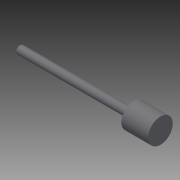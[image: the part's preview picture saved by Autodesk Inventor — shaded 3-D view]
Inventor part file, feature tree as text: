
AUTODESK INVENTOR PART (.ipt)
format: ipt  version: 2014 (Build 180170000, 170)  size: 115,712 bytes
history: native  units: in
note: dims shown in document units (in); Inventor stores cm internally (conversion verified against a paired STEP export)
features: other x49, revolve x2, sketch x2
ambient origin geometry x8: Origin, YZ Plane, XZ Plane, XY Plane, X Axis, Y Axis, Z Axis, Center Point
bodies: Solid1 (feature_tree)
feature tree (53):
  revolve  "Revolution1"  Angle=360.0deg
  revolve  "Revolution2"  [1 undecoded]
  other  "h1_XY"
  other  "h1_YZ"
  other  "h1_ZX"
  other  "h1_X"
  other  "h1_Y"
  other  "h1_Z"
  other  "h1_Center"
  other  "h2_XY"
  other  "h2_YZ"
  other  "h2_ZX"
  other  "h2_X"
  other  "h2_Y"
  other  "h2_Z"
  other  "h2_Center"
  other  "k1_XY"
  other  "k1_YZ"
  other  "k1_ZX"
  other  "k1_X"
  other  "k1_Y"
  other  "k1_Z"
  other  "k1_Center"
  other  "k2_XY"
  other  "k2_YZ"
  other  "k2_ZX"
  other  "k2_X"
  other  "k2_Y"
  other  "k2_Z"
  other  "k2_Center"
  other  "start_XY"
  other  "start_YZ"
  other  "start_ZX"
  other  "start_X"
  other  "start_Y"
  other  "start_Z"
  other  "start_Center"
  other  "to_prc_XY"
  other  "to_prc_YZ"
  other  "to_prc_ZX"
  other  "to_prc_X"
  other  "to_prc_Y"
  other  "to_prc_Z"
  other  "to_prc_Center"
  other  "to_rod_guide_XY"
  other  "to_rod_guide_YZ"
  other  "to_rod_guide_ZX"
  other  "to_rod_guide_X"
  other  "to_rod_guide_Y"
  other  "to_rod_guide_Z"
  other  "to_rod_guide_Center"
  sketch  "Sketch_5"  dims[d0=360.0deg d1=360.0deg]
  sketch  "Sketch_14"
note: 1 required parameter value undecoded (feature->parameter linkage not recoverable at this tier; creation-order binding heuristic only, values carry confidence <= 0.55)
